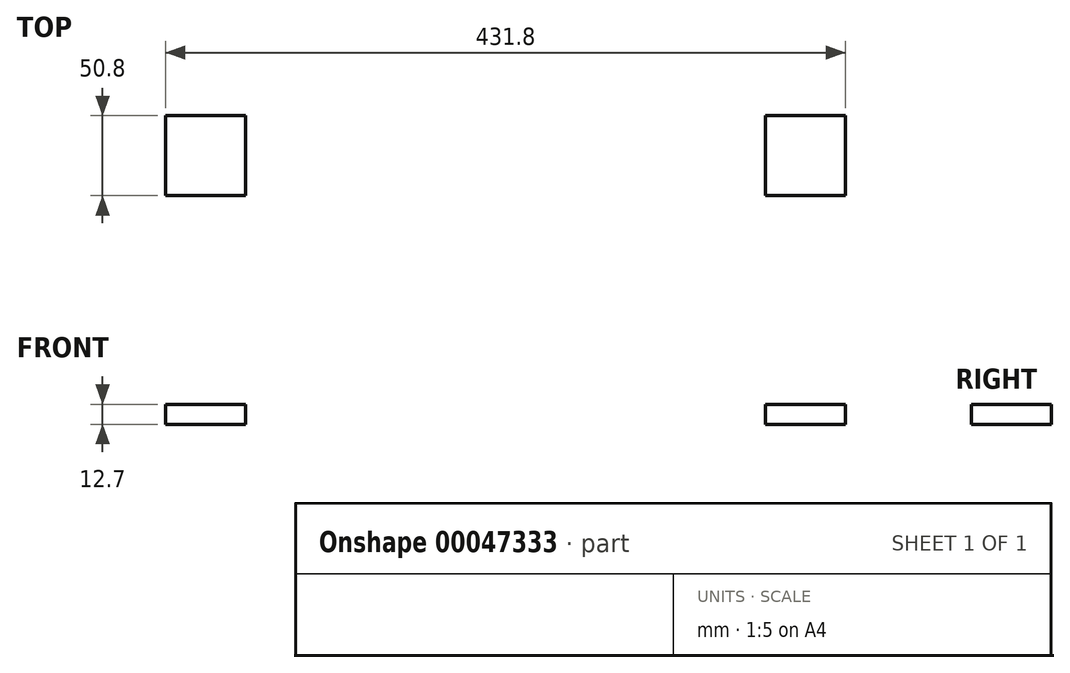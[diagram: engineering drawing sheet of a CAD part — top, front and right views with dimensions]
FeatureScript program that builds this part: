
annotation { "Feature Type Name" : "Feature", "Feature Type Description" : "" }
export const myFeature = defineFeature(function(context is Context, id is Id, definition is map)
    precondition{}
    {
        {
            var Q0;
            Q0=qCreatedBy(makeId("Top.planeOp"),FACE);
            var sketch = newSketch(context, id + "F0", { "sketchPlane" : qUnion([Q0])});
            skLineSegment(sketch, "E0.bottom", {"start": v(-36.94, 313.7) * mm, "end": v(394.86, 313.7) * mm});
            skLineSegment(sketch, "E0.top", {"start": v(-36.94, -16.5) * mm, "end": v(394.86, -16.5) * mm});
            skLineSegment(sketch, "E0.left", {"start": v(-36.94, 313.7) * mm, "end": v(-36.94, -16.5) * mm});
            skLineSegment(sketch, "E0.right", {"start": v(394.86, 313.7) * mm, "end": v(394.86, -16.5) * mm});
            skLineSegment(sketch, "E1.bottom", {"start": v(-36.94, 313.7) * mm, "end": v(13.86, 313.7) * mm});
            skLineSegment(sketch, "E1.top", {"start": v(-36.94, 262.9) * mm, "end": v(13.86, 262.9) * mm});
            skLineSegment(sketch, "E1.left", {"start": v(-36.94, 313.7) * mm, "end": v(-36.94, 262.9) * mm});
            skLineSegment(sketch, "E1.right", {"start": v(13.86, 313.7) * mm, "end": v(13.86, 262.9) * mm});
            skLineSegment(sketch, "E2.bottom", {"start": v(-36.94, -16.5) * mm, "end": v(13.86, -16.5) * mm});
            skLineSegment(sketch, "E2.top", {"start": v(-36.94, 34.3) * mm, "end": v(13.86, 34.3) * mm});
            skLineSegment(sketch, "E2.left", {"start": v(-36.94, -16.5) * mm, "end": v(-36.94, 34.3) * mm});
            skLineSegment(sketch, "E2.right", {"start": v(13.86, -16.5) * mm, "end": v(13.86, 34.3) * mm});
            skLineSegment(sketch, "E3.bottom", {"start": v(394.86, 313.7) * mm, "end": v(344.06, 313.7) * mm});
            skLineSegment(sketch, "E3.top", {"start": v(394.86, 262.9) * mm, "end": v(344.06, 262.9) * mm});
            skLineSegment(sketch, "E3.left", {"start": v(394.86, 313.7) * mm, "end": v(394.86, 262.9) * mm});
            skLineSegment(sketch, "E3.right", {"start": v(344.06, 313.7) * mm, "end": v(344.06, 262.9) * mm});
            skLineSegment(sketch, "E4.bottom", {"start": v(394.86, -16.5) * mm, "end": v(344.06, -16.5) * mm});
            skLineSegment(sketch, "E4.top", {"start": v(394.86, 34.3) * mm, "end": v(344.06, 34.3) * mm});
            skLineSegment(sketch, "E4.left", {"start": v(394.86, -16.5) * mm, "end": v(394.86, 34.3) * mm});
            skLineSegment(sketch, "E4.right", {"start": v(344.06, -16.5) * mm, "end": v(344.06, 34.3) * mm});
            skSolve(sketch);
        }
        {
            var Q0;
            Q0=makeQuery(id+"F0.imprint","IMPRINT",FACE,{"disambiguationData":[TD([[makeQuery(id+"F0.imprint","IMPRINT",EDGE,{"derivedFrom":sQuery(id+"F0.wireOp",EDGE,"E0.bottom")}),-1.0]])]});
            extrude(context, id + "F1", {"entities" : qUnion([Q0]), "depth" : 12.7 * mm});
        }
    });
